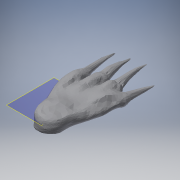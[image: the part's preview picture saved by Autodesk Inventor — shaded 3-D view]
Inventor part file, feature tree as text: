
AUTODESK INVENTOR PART (.ipt)
format: ipt  version: 2019 (Build 230136000, 136)  size: 6,963,712 bytes
history: native  units: in
note: dims shown in document units (in); Inventor stores cm internally (conversion verified against a paired STEP export)
features: other x6, reference x4, plane x1, extrude x1, sketch x1
ambient origin geometry x8: Origin, YZ Plane, XZ Plane, XY Plane, X Axis, Y Axis, Z Axis, Center Point
bodies: Solid1 (feature_tree)
feature tree (13):
  other  "MudBox Foot R.ipt"
  plane  "Work Plane1"
  extrude  "Extrusion1"  Depth=0.0087in TaperAngle=0.0deg
  other  "Solid1::MudBox Foot R.ipt"
  other  "TaggingFeature1"
  sketch  "Sketch1"  dims[d0=0.0087in d1=3.0in d2=0.0in]
  reference  "Reference1"
  reference  "Reference2"
  reference  "Reference3"
  reference  "Reference4"
  other  "Assembled Mudbox Claw R.iam"
  other  "temp:1"
  other  "Assembly1"
